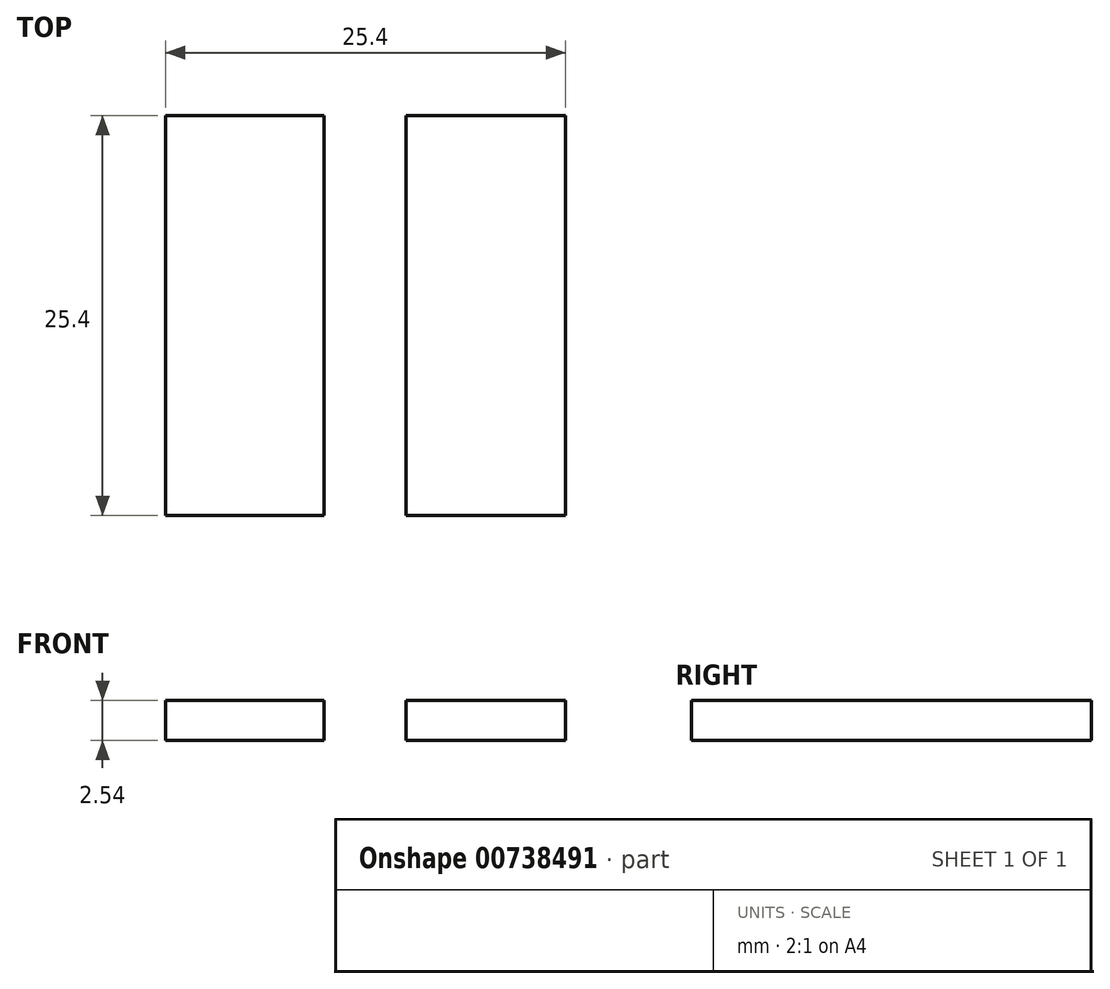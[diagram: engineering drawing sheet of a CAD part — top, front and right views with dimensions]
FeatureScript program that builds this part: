
annotation { "Feature Type Name" : "Feature", "Feature Type Description" : "" }
export const myFeature = defineFeature(function(context is Context, id is Id, definition is map)
    precondition{}
    {
        {
            var Q0;
            Q0=qCreatedBy(makeId("Top.planeOp"),FACE);
            var sketch = newSketch(context, id + "F0", { "sketchPlane" : qUnion([Q0])});
            skLineSegment(sketch, "E0.bottom", {"start": v(-72, 72.2) * mm, "end": v(29.6, 72.2) * mm});
            skLineSegment(sketch, "E0.top", {"start": v(-72, -29.4) * mm, "end": v(29.6, -29.4) * mm});
            skLineSegment(sketch, "E0.left", {"start": v(-72, 72.2) * mm, "end": v(-72, -29.4) * mm});
            skLineSegment(sketch, "E0.right", {"start": v(29.6, 72.2) * mm, "end": v(29.6, -29.4) * mm});
            skSolve(sketch);
        }
        {
            var Q0;
            Q0=makeQuery(id+"F0.imprint","IMPRINT",FACE,{"disambiguationData":[TD([[makeQuery(id+"F0.imprint","IMPRINT",EDGE,{"derivedFrom":sQuery(id+"F0.wireOp",EDGE,"E0.bottom")}),-1.0]])]});
            extrude(context, id + "F1", {"entities" : qUnion([Q0]), "depth" : 10.16 * mm, "offsetDistance" : 25.4 * mm});
        }
        {
            var Q0;
            Q0=makeQuery(id+"F1.opExtrude","CAP_FACE",FACE,{"disambiguationData":[OSD([sQuery(id+"F0.wireOp",EDGE,"E0.bottom"),sQuery(id+"F0.wireOp",EDGE,"E0.top"),sQuery(id+"F0.wireOp",EDGE,"E0.left"),sQuery(id+"F0.wireOp",EDGE,"E0.right")])],"isStart":false});
            var sketch = newSketch(context, id + "F2", { "sketchPlane" : qUnion([Q0])});
            skLineSegment(sketch, "E1", {"start": v(-21.2, -29.4) * mm, "end": v(-21.2, 72.2) * mm});
            skLineSegment(sketch, "E2", {"start": v(-72, 21.4) * mm, "end": v(29.6, 21.4) * mm});
            skLineSegment(sketch, "E3.bottom", {"start": v(-31.77, -29.4) * mm, "end": v(-10.97, -29.4) * mm});
            skLineSegment(sketch, "E3.top", {"start": v(-31.77, 72.2) * mm, "end": v(-10.97, 72.2) * mm});
            skLineSegment(sketch, "E3.left", {"start": v(-31.77, -29.4) * mm, "end": v(-31.77, 72.2) * mm});
            skLineSegment(sketch, "E3.right", {"start": v(-10.97, -29.4) * mm, "end": v(-10.97, 72.2) * mm});
            skSolve(sketch);
        }
        {
            var Q0;
            {var subQ0=sQuery(id+"F2.wireOp",EDGE,"E3.bottom");var subQ1=sQuery(id+"F2.wireOp",EDGE,"E1");var subQ2=makeQuery(id+"F2.imprint","INTERSECT",VERTEX,{"derivedFrom":[subQ1,subQ0]});Q0=makeQuery(id+"F2.imprint","IMPRINT",FACE,{"disambiguationData":[TD([[makeQuery(id+"F2.imprint","IMPRINT",EDGE,{"disambiguationData":[TD([[subQ2,-1.0]])],"derivedFrom":subQ1}),-1.0]])]});}
            var Q1;
            {var subQ0=sQuery(id+"F2.wireOp",EDGE,"E3.bottom");var subQ1=sQuery(id+"F2.wireOp",EDGE,"E1");var subQ2=makeQuery(id+"F2.imprint","INTERSECT",VERTEX,{"derivedFrom":[subQ1,subQ0]});Q1=makeQuery(id+"F2.imprint","IMPRINT",FACE,{"disambiguationData":[TD([[makeQuery(id+"F2.imprint","IMPRINT",EDGE,{"disambiguationData":[TD([[subQ2,-1.0]])],"derivedFrom":subQ1}),1.0]])]});}
            var Q2;
            {var subQ0=sQuery(id+"F2.wireOp",EDGE,"E3.top");var subQ1=sQuery(id+"F2.wireOp",EDGE,"E1");var subQ2=makeQuery(id+"F2.imprint","INTERSECT",VERTEX,{"derivedFrom":[subQ1,subQ0]});Q2=makeQuery(id+"F2.imprint","IMPRINT",FACE,{"disambiguationData":[TD([[makeQuery(id+"F2.imprint","IMPRINT",EDGE,{"disambiguationData":[TD([[subQ2,1.0]])],"derivedFrom":subQ1}),1.0]])]});}
            var Q3;
            {var subQ0=sQuery(id+"F2.wireOp",EDGE,"E3.top");var subQ1=sQuery(id+"F2.wireOp",EDGE,"E1");var subQ2=makeQuery(id+"F2.imprint","INTERSECT",VERTEX,{"derivedFrom":[subQ1,subQ0]});Q3=makeQuery(id+"F2.imprint","IMPRINT",FACE,{"disambiguationData":[TD([[makeQuery(id+"F2.imprint","IMPRINT",EDGE,{"disambiguationData":[TD([[subQ2,1.0]])],"derivedFrom":subQ1}),-1.0]])]});}
            extrude(context, id + "F3", {"entities" : qUnion([Q0, Q1, Q2, Q3]), "operationType" : NewBodyOperationType.REMOVE, "oppositeDirection" : true, "depth" : 25.4 * mm, "offsetDistance" : 25.4 * mm});
        }
        {
            var Q0;
            Q0=makeQuery(id+"F3.boolean.opBoolean","SPLIT",BODY,{"disambiguationData":[OD(0.0)],"derivedFrom":makeQuery(id+"F1.opExtrude","SWEPT_BODY",BODY,{"disambiguationData":[OSD([sQuery(id+"F0.wireOp",EDGE,"E0.bottom"),sQuery(id+"F0.wireOp",EDGE,"E0.top"),sQuery(id+"F0.wireOp",EDGE,"E0.left"),sQuery(id+"F0.wireOp",EDGE,"E0.right")])]})});
            var Q1;
            Q1=makeQuery(id+"F3.boolean.opBoolean","SPLIT",BODY,{"disambiguationData":[OD(1.0)],"derivedFrom":makeQuery(id+"F1.opExtrude","SWEPT_BODY",BODY,{"disambiguationData":[OSD([sQuery(id+"F0.wireOp",EDGE,"E0.bottom"),sQuery(id+"F0.wireOp",EDGE,"E0.top"),sQuery(id+"F0.wireOp",EDGE,"E0.left"),sQuery(id+"F0.wireOp",EDGE,"E0.right")])]})});
            var Q2;
            Q2=makeQuery(id+"F3.boolean.opBoolean","COPY",VERTEX,{"derivedFrom":makeQuery(id+"F3.opExtrude","CAP_VERTEX",VERTEX,{"disambiguationData":[OSD([sQuery(id+"F0.wireOp",EDGE,"E0.top"),sQuery(id+"F2.wireOp",EDGE,"E3.bottom"),sQuery(id+"F2.wireOp",EDGE,"E3.right")])],"isStart":true})});
            transform(context, id + "F4", {"entities" : qUnion([Q0, Q1]), "transformType" : TransformType.SCALE_UNIFORMLY, "scale" : .25, "scalePoint" : qUnion([Q2]), "makeCopy" : false});
        }
    });
